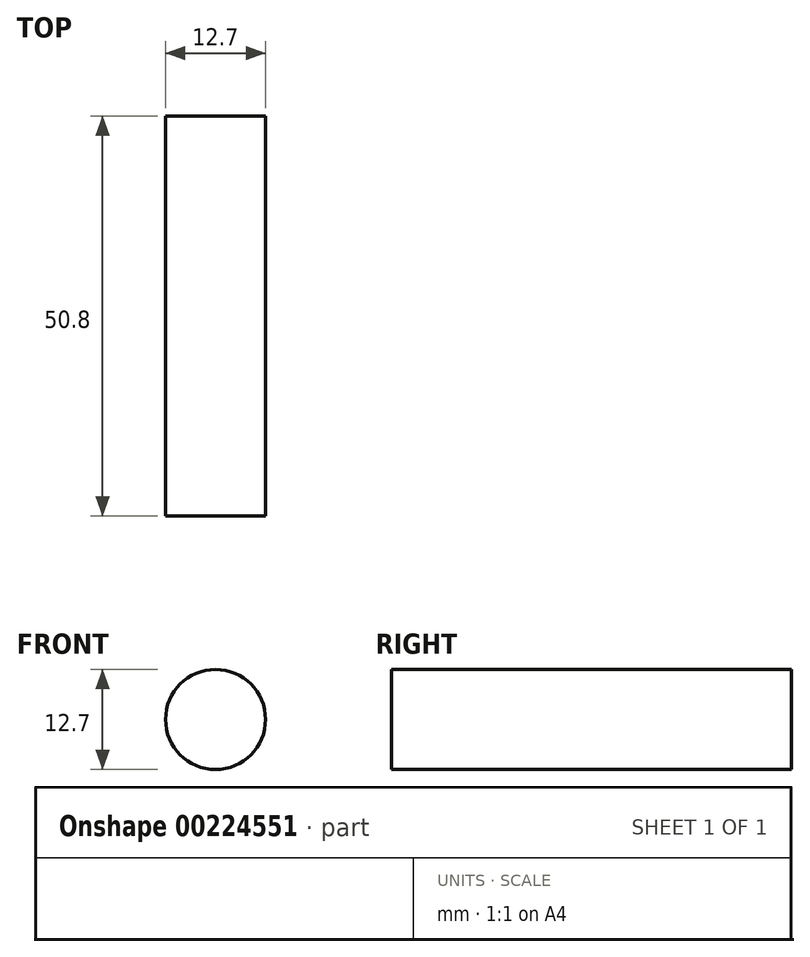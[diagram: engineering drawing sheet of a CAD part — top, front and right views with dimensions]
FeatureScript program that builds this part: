
annotation { "Feature Type Name" : "Feature", "Feature Type Description" : "" }
export const myFeature = defineFeature(function(context is Context, id is Id, definition is map)
    precondition{}
    {
        {
            var Q0;
            Q0=qCreatedBy(makeId("Front.planeOp"),FACE);
            var sketch = newSketch(context, id + "F0", { "sketchPlane" : qUnion([Q0])});
            skCircle(sketch, "E0", {"center": v(-52.48, 34.99) * mm, "radius": 6.35 * mm});
            skSolve(sketch);
        }
        {
            var Q0;
            Q0=makeQuery(id+"F0.imprint","IMPRINT",FACE,{"disambiguationData":[TD([[makeQuery(id+"F0.imprint","IMPRINT",EDGE,{"derivedFrom":sQuery(id+"F0.wireOp",EDGE,"E0")}),1.0]])]});
            extrude(context, id + "F1", {"entities" : qUnion([Q0]), "depth" : 50.8 * mm});
        }
    });
